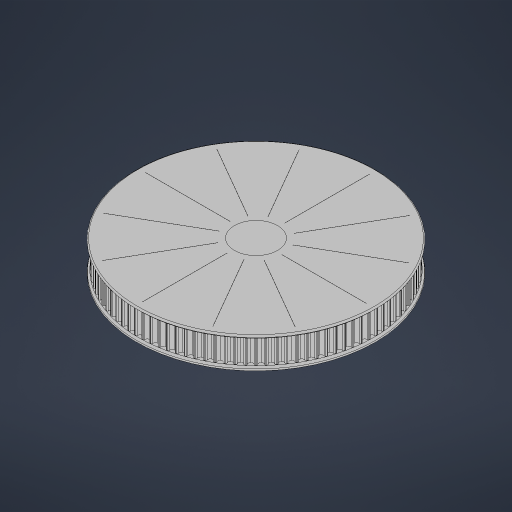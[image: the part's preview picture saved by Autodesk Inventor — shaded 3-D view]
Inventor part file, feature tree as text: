
AUTODESK INVENTOR PART (.ipt)
format: ipt  version: 2024 (Build 280153000, 153)  size: 1,333,248 bytes
history: native  units: mm
features: extrude x4, fillet x3, sketch x3, pattern_circular x2, revolve x1, mirror x1
ambient origin geometry x8: Origin, YZ Plane, XZ Plane, XY Plane, X Axis, Y Axis, Z Axis, Center Point
bodies: Solid1 (feature_tree)
feature tree (14):
  extrude  "Extrusion1"  Depth=21.0mm
  extrude  "Extrusion2"  Depth=5.8mm
  extrude  "Extrusion3"  Depth=21.0mm
  fillet  "Fillet2"  [1 undecoded]
  pattern_circular  "Circular Pattern1"  [2 undecoded]
  revolve  "Revolution2"  [1 undecoded]
  mirror  "Mirror2"
  fillet  "Fillet5"  [1 undecoded]
  extrude  "Extrusion4"  Depth=0.6mm
  pattern_circular  "Circular Pattern2"  Count=100  [1 undecoded]
  fillet  "Fillet1"  [1 undecoded]
  sketch  "Sketch2"  dims[d0=29.0mm d2=21.0mm]
  sketch  "Sketch5"  dims[d3=0.0mm d5=5.8mm]
  sketch  "Sketch6"  dims[d7=1.565mm d8=21.0mm d9=0.0mm d10=0.6mm d12=159.154943mm d13=0.0mm d14=0.0mm d15=0.6mm d16=1000.0mm d17=360.0deg d35=90.0deg d36=0.0mm d37=2.5mm d38=76.577472mm d39=5.1mm d40=2.5mm d41=2.5mm d42=0.8mm d43=0.05mm d44=75.577472mm d45=18.5mm d46=10.0mm d47=0.0mm d48=120.0mm d49=360.0deg]
note: 7 required parameter values undecoded (feature->parameter linkage not recoverable at this tier; creation-order binding heuristic only, values carry confidence <= 0.55)